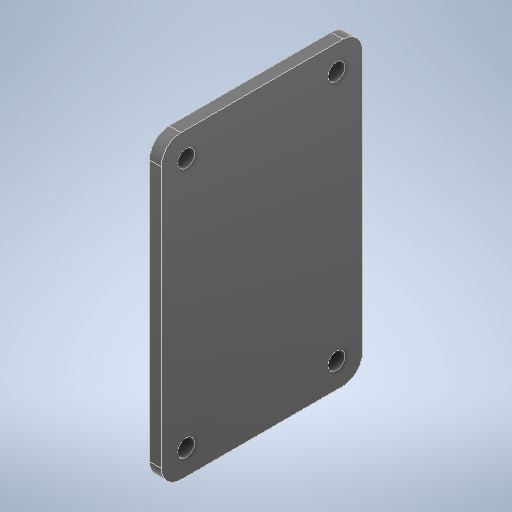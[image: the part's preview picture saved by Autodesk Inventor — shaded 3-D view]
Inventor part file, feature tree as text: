
AUTODESK INVENTOR PART (.ipt)
format: ipt  version: 2025.1 (Build 291241020, 241B)  size: 272,384 bytes
history: native  units: mm
features: plane x4, extrude x1, fillet x1, other x1, hole x1
ambient origin geometry x8: Origin, YZ Plane, XZ Plane, XY Plane, X Axis, Y Axis, Z Axis, Center Point
bodies: Solid1 (feature_tree)
feature tree (8):
  extrude  "Body Extrude"  Depth=3.0mm TaperAngle=0.0deg
  plane  "Work Plane1"
  plane  "Work Plane2"
  plane  "Work Plane3"
  plane  "Work Plane4"
  fillet  "Fillet2"  Radius=76.2mm
  other  "Body Sketch"
  hole  "Hole Sketch"  [1 undecoded]
note: 1 required parameter value undecoded (feature->parameter linkage not recoverable at this tier; creation-order binding heuristic only, values carry confidence <= 0.55)
